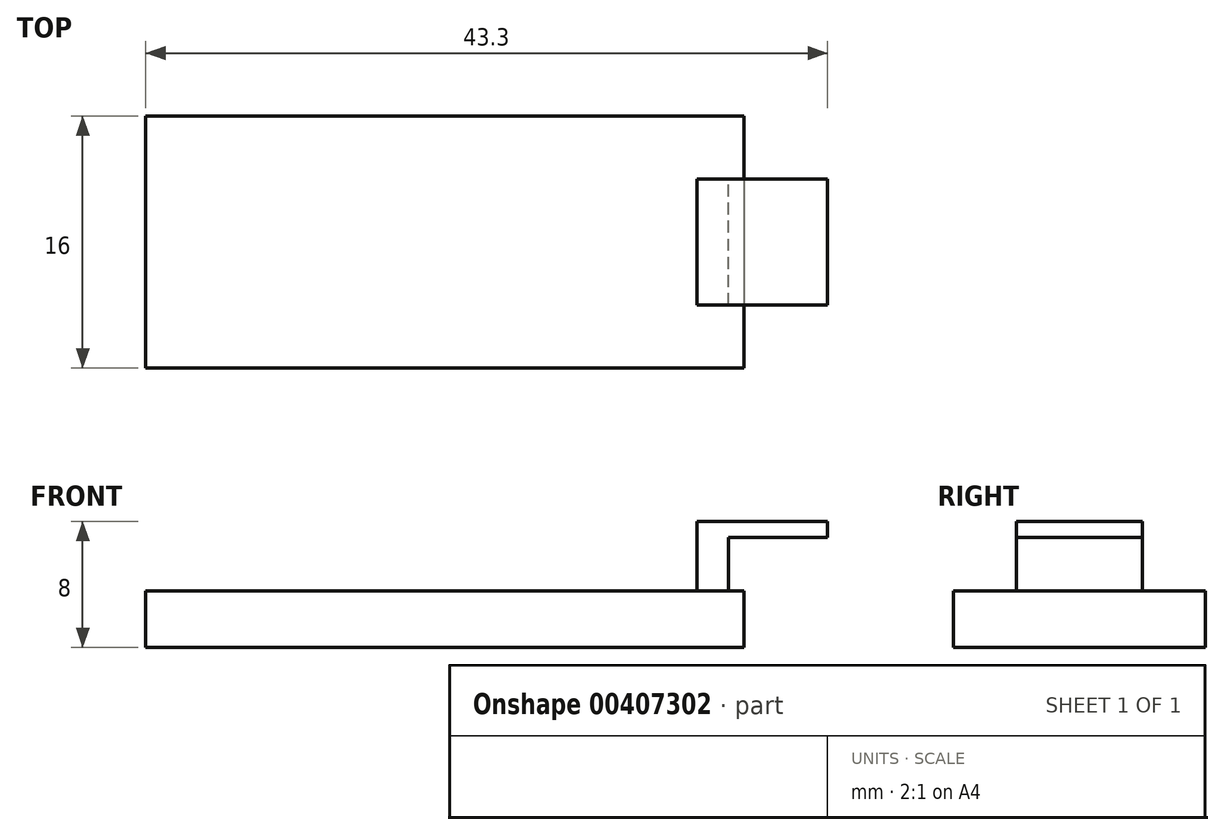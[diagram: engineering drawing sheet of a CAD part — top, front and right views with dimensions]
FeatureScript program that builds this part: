
annotation { "Feature Type Name" : "Feature", "Feature Type Description" : "" }
export const myFeature = defineFeature(function(context is Context, id is Id, definition is map)
    precondition{}
    {
        {
            var Q0;
            Q0=qCreatedBy(makeId("Top.planeOp"),FACE);
            var sketch = newSketch(context, id + "F0", { "sketchPlane" : qUnion([Q0])});
            skLineSegment(sketch, "E0.bottom", {"start": v(0, 0) * mm, "end": v(38, 0) * mm});
            skLineSegment(sketch, "E0.top", {"start": v(0, -16) * mm, "end": v(38, -16) * mm});
            skLineSegment(sketch, "E0.left", {"start": v(0, 0) * mm, "end": v(0, -16) * mm});
            skLineSegment(sketch, "E0.right", {"start": v(38, 0) * mm, "end": v(38, -16) * mm});
            skSolve(sketch);
        }
        {
            var Q0;
            Q0 = qSketchRegion(id + "F0", true);
            extrude(context, id + "F1", {"entities" : qUnion([Q0]), "depth" : 3.6 * mm});
        }
        {
            var Q0;
            Q0=qCreatedBy(makeId("Top.planeOp"),FACE);
            cPlane(context, id + "F2", {"entities" : qUnion([Q0]), "cplaneType" : CPlaneType.OFFSET, "offset" : 3.6 * mm, "width" : 150 * mm, "height" : 150 * mm});
        }
        {
            var Q0;
            Q0=qCreatedBy(id+"F2.planeOp",FACE);
            var sketch = newSketch(context, id + "F3", { "sketchPlane" : qUnion([Q0])});
            skLineSegment(sketch, "E1", {"start": v(35, -4) * mm, "end": v(35, -12) * mm});
            skLineSegment(sketch, "E2", {"start": v(37, -8) * mm, "end": v(37, -4) * mm});
            skLineSegment(sketch, "E3", {"start": v(37, -4) * mm, "end": v(35, -4) * mm});
            skLineSegment(sketch, "E4.MirrorCS", {"start": v(37, -8) * mm, "end": v(37, -12) * mm});
            skLineSegment(sketch, "E5.MirrorCS", {"start": v(37, -12) * mm, "end": v(35, -12) * mm});
            skSolve(sketch);
        }
        {
            var Q0;
            Q0=makeQuery(id+"F3.imprint","IMPRINT",FACE,{"disambiguationData":[TD([[makeQuery(id+"F3.imprint","IMPRINT",EDGE,{"derivedFrom":sQuery(id+"F3.wireOp",EDGE,"E1")}),1.0]])]});
            extrude(context, id + "F4", {"entities" : qUnion([Q0]), "operationType" : NewBodyOperationType.ADD, "depth" : 3.4 * mm});
        }
        {
            var Q0;
            Q0=qCreatedBy(id+"F2.planeOp",FACE);
            cPlane(context, id + "F5", {"entities" : qUnion([Q0]), "cplaneType" : CPlaneType.OFFSET, "offset" : 3.4 * mm, "width" : 150 * mm, "height" : 150 * mm});
        }
        {
            var Q0;
            Q0=qCreatedBy(id+"F5.planeOp",FACE);
            var sketch = newSketch(context, id + "F6", { "sketchPlane" : qUnion([Q0])});
            skLineSegment(sketch, "E6", {"start": v(43.3, -8) * mm, "end": v(43.3, -4) * mm});
            skLineSegment(sketch, "E7", {"start": v(43.3, -4) * mm, "end": v(35, -4) * mm});
            skLineSegment(sketch, "E8.MirrorCS", {"start": v(43.3, -8) * mm, "end": v(43.3, -12) * mm});
            skLineSegment(sketch, "E9.MirrorCS", {"start": v(43.3, -12) * mm, "end": v(35, -12) * mm});
            skLineSegment(sketch, "E10", {"start": v(35, -4) * mm, "end": v(35, -12) * mm});
            skSolve(sketch);
        }
        {
            var Q0;
            Q0 = qSketchRegion(id + "F6", true);
            extrude(context, id + "F7", {"entities" : qUnion([Q0]), "operationType" : NewBodyOperationType.ADD, "depth" : 1 * mm});
        }
    });
